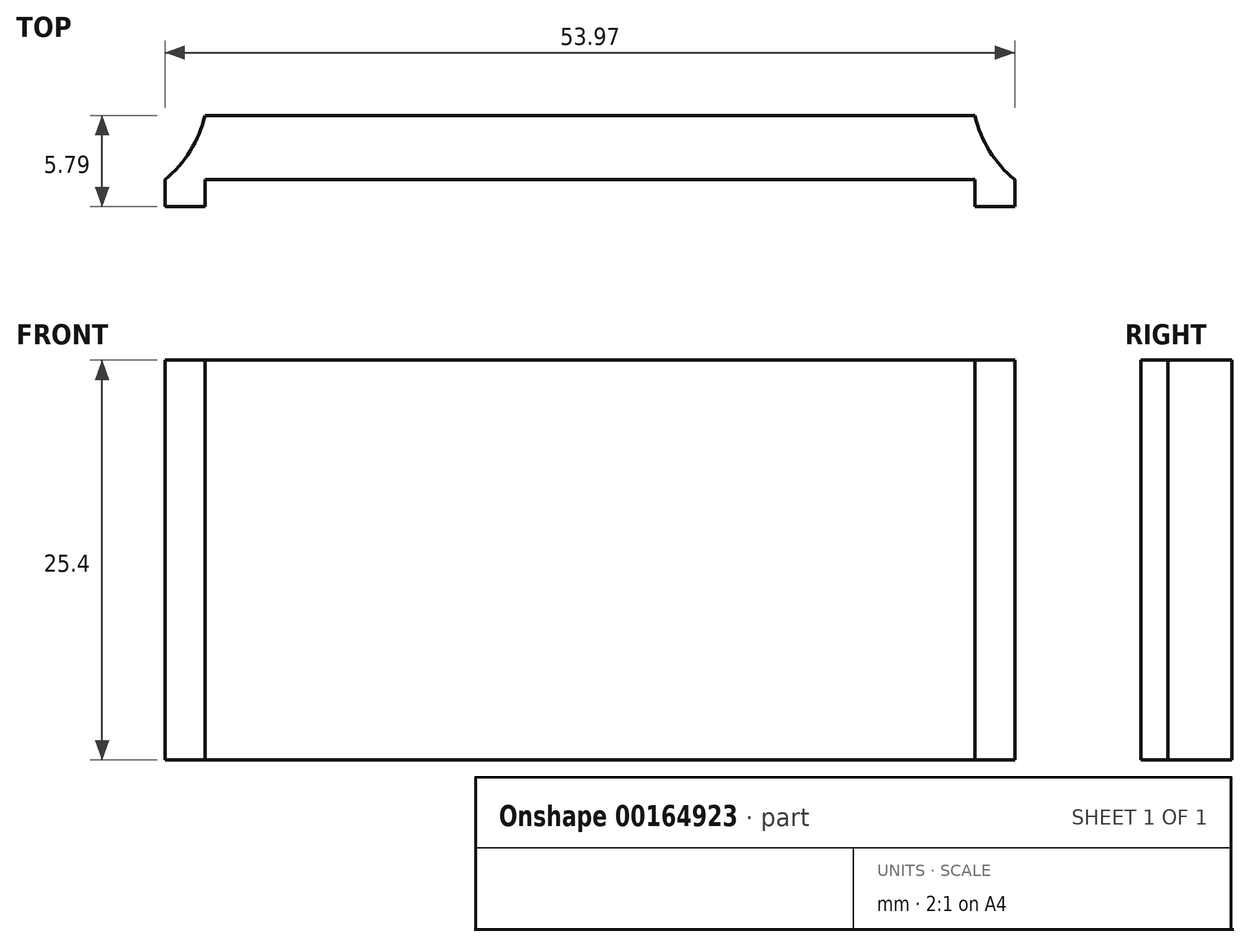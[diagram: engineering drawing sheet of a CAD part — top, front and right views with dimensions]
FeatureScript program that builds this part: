
annotation { "Feature Type Name" : "Feature", "Feature Type Description" : "" }
export const myFeature = defineFeature(function(context is Context, id is Id, definition is map)
    precondition{}
    {
        {
            var Q0;
            Q0=qCreatedBy(makeId("Top.planeOp"),FACE);
            var sketch = newSketch(context, id + "F0", { "sketchPlane" : qUnion([Q0])});
            skLineSegment(sketch, "E0", {"start": v(0, 0) * mm, "end": v(0, 1.7) * mm});
            skLineSegment(sketch, "E1", {"start": v(0, 0) * mm, "end": v(-4.77, 0) * mm, "construction": true});
            skArc(sketch, "E2", {"start": v(-4.77, 0) * mm, "mid": v(-2.23, 0.44) * mm, "end": v(0, 1.7) * mm, "construction": true});
            skArc(sketch, "E3", {"start": v(0, 1.7) * mm, "mid": v(1.6, 3.54) * mm, "end": v(2.54, 5.8) * mm});
            skLineSegment(sketch, "E4", {"start": v(-4.77, 7.5) * mm, "end": v(58.73, 7.5) * mm, "construction": true});
            skLineSegment(sketch, "E5", {"start": v(2.54, 5.8) * mm, "end": v(51.43, 5.8) * mm});
            skLineSegment(sketch, "E6", {"start": v(26.98, 7.5) * mm, "end": v(26.98, 5.8) * mm, "construction": true});
            skArc(sketch, "E7", {"start": v(51.43, 5.8) * mm, "mid": v(52.36, 3.54) * mm, "end": v(53.97, 1.7) * mm});
            skLineSegment(sketch, "E8", {"start": v(53.97, 0) * mm, "end": v(53.97, 1.7) * mm});
            skLineSegment(sketch, "E9", {"start": v(53.97, 0) * mm, "end": v(51.43, 0) * mm});
            skLineSegment(sketch, "E10", {"start": v(51.43, 0) * mm, "end": v(51.43, 1.7) * mm});
            skLineSegment(sketch, "E11", {"start": v(51.43, 1.7) * mm, "end": v(2.54, 1.7) * mm});
            skLineSegment(sketch, "E12", {"start": v(2.54, 1.7) * mm, "end": v(2.54, 0) * mm});
            skLineSegment(sketch, "E13", {"start": v(2.54, 0) * mm, "end": v(0, 0) * mm});
            skSolve(sketch);
        }
        {
            var Q0;
            Q0 = qSketchRegion(id + "F0", true);
            extrude(context, id + "F1", {"entities" : qUnion([Q0]), "depth" : 25.4 * mm});
        }
    });
